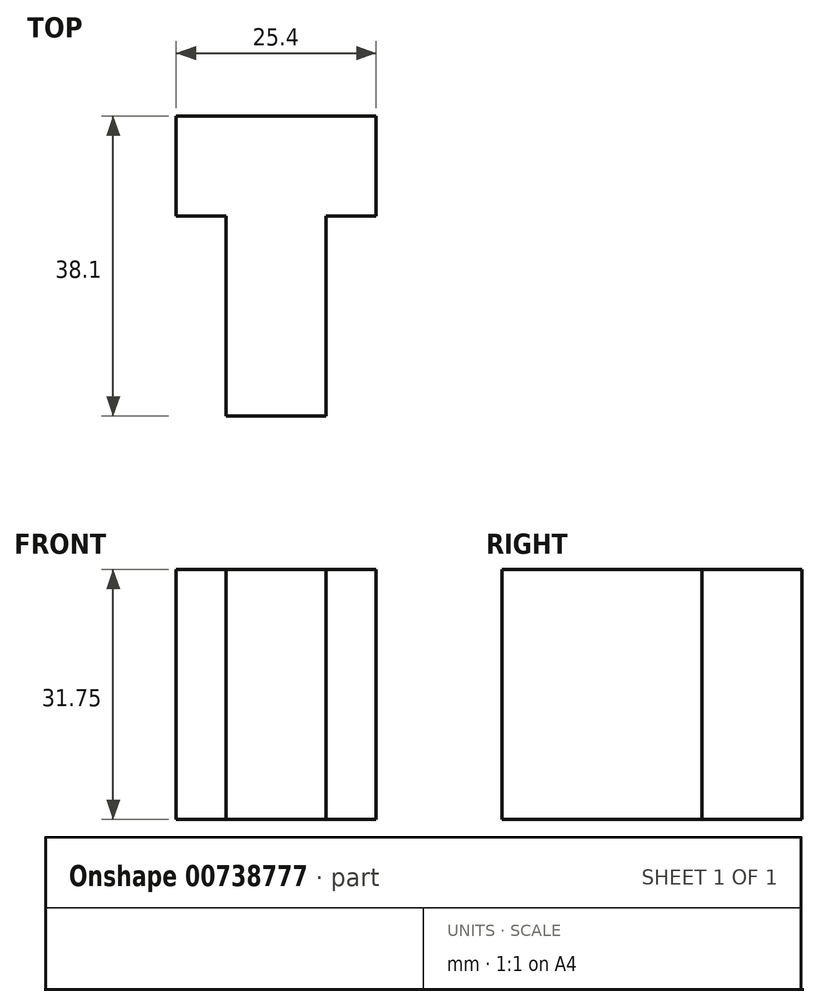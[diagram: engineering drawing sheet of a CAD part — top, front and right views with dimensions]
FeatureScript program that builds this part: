
annotation { "Feature Type Name" : "Feature", "Feature Type Description" : "" }
export const myFeature = defineFeature(function(context is Context, id is Id, definition is map)
    precondition{}
    {
        {
            var Q0;
            Q0=qCreatedBy(makeId("Top.planeOp"),FACE);
            var sketch = newSketch(context, id + "F0", { "sketchPlane" : qUnion([Q0])});
            skLineSegment(sketch, "E0", {"start": v(25.5, 0) * mm, "end": v(25.5, 25.4) * mm});
            skLineSegment(sketch, "E1", {"start": v(25.5, 25.4) * mm, "end": v(19.15, 25.4) * mm});
            skLineSegment(sketch, "E2", {"start": v(19.15, 25.4) * mm, "end": v(19.15, 38.1) * mm});
            skLineSegment(sketch, "E3", {"start": v(19.15, 38.1) * mm, "end": v(44.55, 38.1) * mm});
            skLineSegment(sketch, "E4", {"start": v(44.55, 38.1) * mm, "end": v(44.55, 25.4) * mm});
            skLineSegment(sketch, "E5", {"start": v(44.55, 25.4) * mm, "end": v(38.2, 25.4) * mm});
            skLineSegment(sketch, "E6", {"start": v(38.2, 25.4) * mm, "end": v(38.2, 0) * mm});
            skLineSegment(sketch, "E7", {"start": v(38.2, 0) * mm, "end": v(25.5, 0) * mm});
            skSolve(sketch);
        }
        {
            var Q0;
            Q0=makeQuery(id+"F0.imprint","IMPRINT",FACE,{"disambiguationData":[TD([[makeQuery(id+"F0.imprint","IMPRINT",EDGE,{"derivedFrom":sQuery(id+"F0.wireOp",EDGE,"E0")}),-1.0]])]});
            extrude(context, id + "F1", {"entities" : qUnion([Q0]), "depth" : 31.75 * mm, "offsetDistance" : 25.4 * mm});
        }
    });
